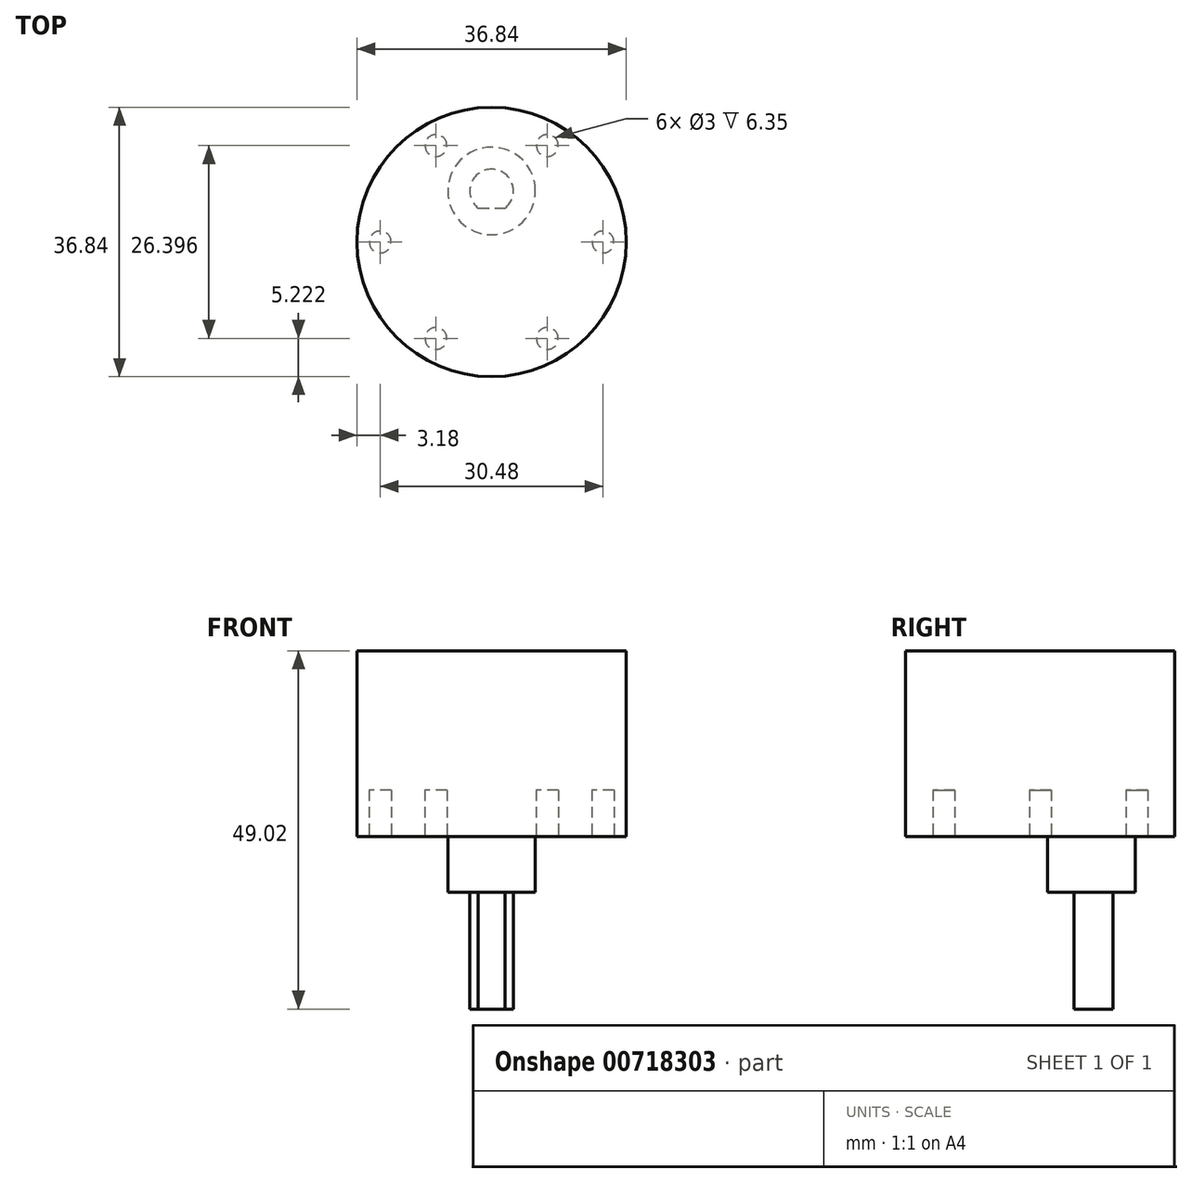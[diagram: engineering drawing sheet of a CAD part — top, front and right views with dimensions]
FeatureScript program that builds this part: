
annotation { "Feature Type Name" : "Feature", "Feature Type Description" : "" }
export const myFeature = defineFeature(function(context is Context, id is Id, definition is map)
    precondition{}
    {
        {
            var Q0;
            Q0=qCreatedBy(makeId("Top.planeOp"),FACE);
            var sketch = newSketch(context, id + "F0", { "sketchPlane" : qUnion([Q0])});
            skCircle(sketch, "E0", {"center": v(0, 0) * mm, "radius": 18.41 * mm});
            skSolve(sketch);
        }
        {
            var Q0;
            Q0=qCreatedBy(makeId("Top.planeOp"),FACE);
            var sketch = newSketch(context, id + "F1", { "sketchPlane" : qUnion([Q0])});
            skLineSegment(sketch, "E1", {"start": v(0, 0) * mm, "end": v(15.24, 0) * mm});
            skPoint(sketch, "E2.center", {"position": v(0, 0) * mm});
            skCircle(sketch, "E3", {"center": v(-15.24, 0) * mm, "radius": 1.5 * mm});
            skCircle(sketch, "E4.1.0", {"center": v(-7.62, -13.2) * mm, "radius": 1.5 * mm});
            skCircle(sketch, "E4.2.0", {"center": v(7.62, -13.2) * mm, "radius": 1.5 * mm});
            skCircle(sketch, "E4.3.0", {"center": v(15.24, 0) * mm, "radius": 1.5 * mm});
            skCircle(sketch, "E4.4.0", {"center": v(7.62, 13.2) * mm, "radius": 1.5 * mm});
            skCircle(sketch, "E4.5.0", {"center": v(-7.62, 13.2) * mm, "radius": 1.5 * mm});
            skSolve(sketch);
        }
        {
            var Q0;
            Q0=qCreatedBy(makeId("Top.planeOp"),FACE);
            var sketch = newSketch(context, id + "F2", { "sketchPlane" : qUnion([Q0])});
            skLineSegment(sketch, "E5", {"start": v(0, 0) * mm, "end": v(0, 6.99) * mm});
            skCircle(sketch, "E6", {"center": v(0, 6.99) * mm, "radius": 6 * mm});
            skSolve(sketch);
        }
        {
            var Q0;
            Q0 = qSketchRegion(id + "F0", true);
            extrude(context, id + "F3", {"entities" : qUnion([Q0]), "depth" : 25.4 * mm, "offsetDistance" : 25.4 * mm});
        }
        {
            var Q0;
            Q0 = qSketchRegion(id + "F1", true);
            extrude(context, id + "F4", {"entities" : qUnion([Q0]), "operationType" : NewBodyOperationType.REMOVE, "depth" : 6.35 * mm, "offsetDistance" : 25.4 * mm});
        }
        {
            var Q0;
            Q0 = qSketchRegion(id + "F2", true);
            extrude(context, id + "F5", {"entities" : qUnion([Q0]), "operationType" : NewBodyOperationType.ADD, "oppositeDirection" : true, "depth" : 7.62 * mm, "offsetDistance" : 25.4 * mm});
        }
        {
            var Q0;
            Q0=makeQuery(id+"F5.opExtrude","CAP_FACE",FACE,{"disambiguationData":[OSD([sQuery(id+"F2.wireOp",EDGE,"E6")])],"isStart":false});
            var sketch = newSketch(context, id + "F6", { "sketchPlane" : qUnion([Q0])});
            skLineSegment(sketch, "E7", {"start": v(0, 0) * mm, "end": v(0, -6.99) * mm});
            skLineSegment(sketch, "E8", {"start": v(0, -4.64) * mm, "end": v(-1.84, -4.64) * mm});
            skLineSegment(sketch, "E9", {"start": v(0, -4.64) * mm, "end": v(1.84, -4.64) * mm});
            skArc(sketch, "E10", {"start": v(-1.84, -4.64) * mm, "mid": v(0, -9.97) * mm, "end": v(1.84, -4.64) * mm});
            skSolve(sketch);
        }
        {
            var Q0;
            Q0 = qSketchRegion(id + "F6", true);
            extrude(context, id + "F7", {"entities" : qUnion([Q0]), "operationType" : NewBodyOperationType.ADD, "depth" : 16 * mm, "offsetDistance" : 25.4 * mm});
        }
    });
